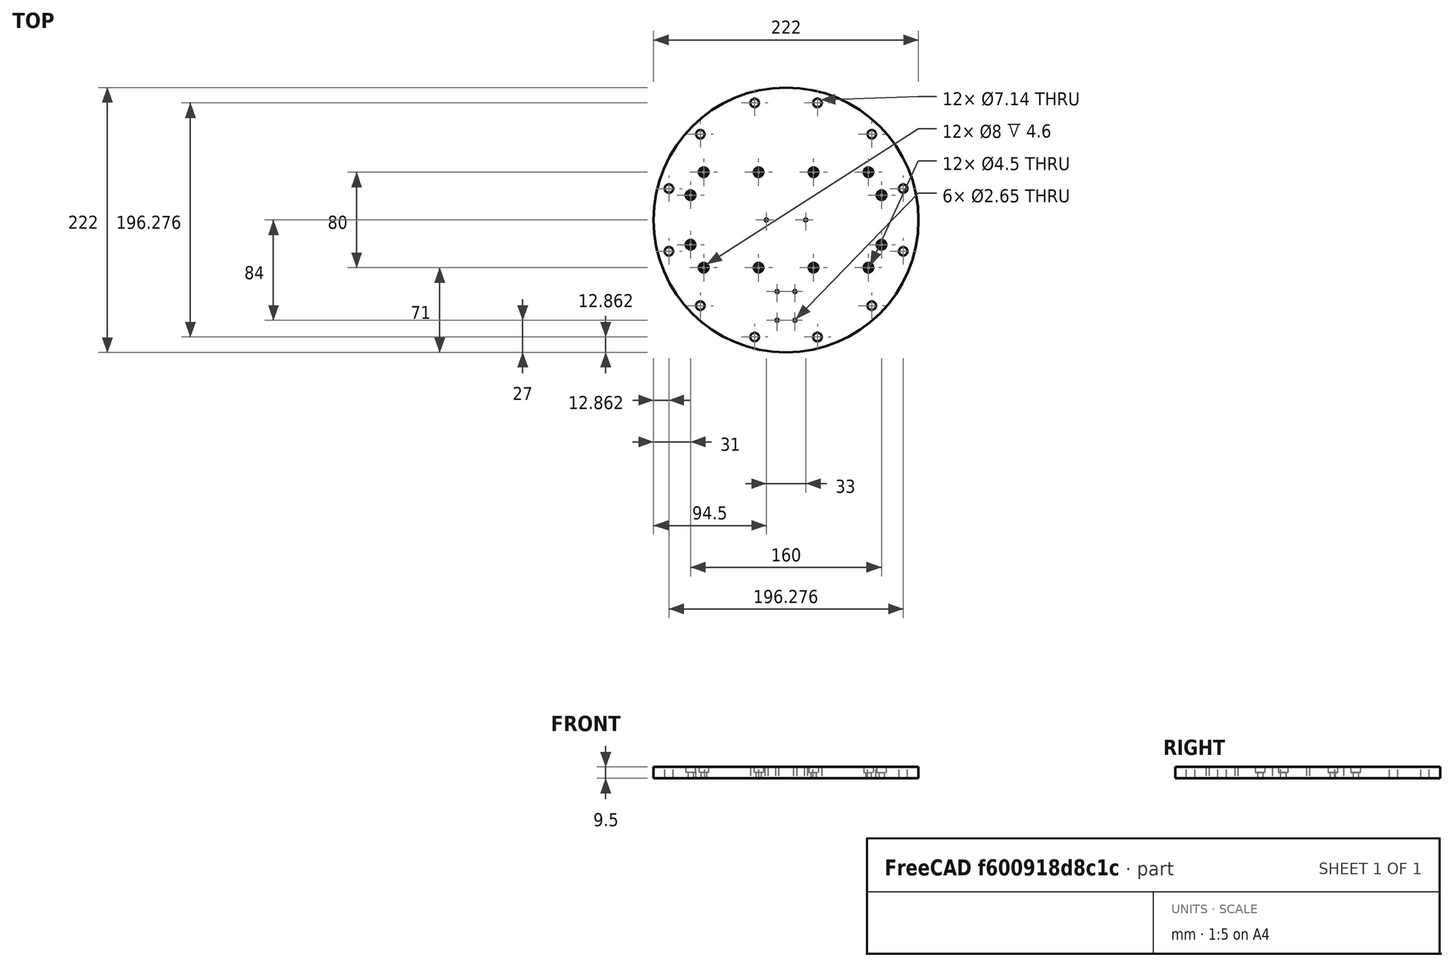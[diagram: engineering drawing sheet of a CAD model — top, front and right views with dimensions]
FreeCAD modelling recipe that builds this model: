
FCSTD DOCUMENT  (FreeCAD 0.19R)
Label: flangle
License: CreativeCommons Attribution-ShareAlike
LicenseURL: http://creativecommons.org/licenses/by-sa/4.0/
objects: TechDraw::DrawViewAnnotation×10, Sketcher::SketchObject×5, PartDesign::Mirrored×4, PartDesign::Hole×3, TechDraw::DrawViewDimension×2, PartDesign::Pad×1, PartDesign::Pocket×1, PartDesign::PolarPattern×1, PartDesign::MultiTransform×1, PartDesign::Body×1, TechDraw::DrawSVGTemplate×1, TechDraw::DrawProjGroupItem×1, TechDraw::DrawProjGroup×1, Spreadsheet::Sheet×1, TechDraw::DrawViewSpreadsheet×1, TechDraw::DrawViewDraft×1, TechDraw::DrawViewPart×1, TechDraw::DrawPage×1
note: 22 computed .brp shape members not serialized (recipe doc carries the construction recipe); baked Part::Feature solids carry a one-line shape summary decoded from their .brp

FEATURE [Sketcher::SketchObject] Sketch
  MapMode = 5
  Support = -> [XY_Plane]
  sketch-geometry (1):
    g0: Circle CenterX=0 CenterY=0 CenterZ=0 NormalX=0 NormalY=0 NormalZ=1 AngleXU=0 Radius=111
  constraints (2):
    c: Coincident(g0,g-1)
    c: Diameter(g0) = 222
FEATURE [PartDesign::Pad] Pad  label="stock"
  Length = 9.5
  Length2 = 100
  Profile = -> Sketch
  Reversed = true
  Type = 0
FEATURE [Sketcher::SketchObject] Sketch001
  MapMode = 5
  Support = -> [XY_Plane]
  sketch-geometry (2):
    g0: Circle CenterX=26.296 CenterY=98.1381 CenterZ=0 NormalX=0 NormalY=0 NormalZ=1 AngleXU=0 Radius=3.57
    g1: LineSegment [constr] StartX=26.296 StartY=98.1381 StartZ=0 EndX=7.1e-15 EndY=0 EndZ=0
  constraints (5):
    c: Diameter(g0) = 7.14
    c: Coincident(g1,g0)
    c: Coincident(g1,g-1)
    c: Angle(g1,g-2) = 0.261799
    c: Distance(g1) = 101.6
FEATURE [PartDesign::Pocket] Pocket  label="mount-hole"
  BaseFeature = -> Pad
  Length = 5
  Length2 = 100
  Profile = -> Sketch001
  Type = 1
FEATURE [PartDesign::PolarPattern] PolarPattern  label="mounting-holes"
  Angle = 360
  Axis = -> Sketch001 [N_Axis]
  BaseFeature = -> Pocket
  Occurrences = 12
  Originals = -> [Pocket]
FEATURE [Sketcher::SketchObject] Sketch002
  MapMode = 5
  Support = -> [XY_Plane]
  sketch-geometry (3):
    g0: Circle CenterX=-80 CenterY=20.75 CenterZ=0 NormalX=0 NormalY=0 NormalZ=1 AngleXU=0 Radius=2.5
    g1: Circle CenterX=-69 CenterY=40 CenterZ=0 NormalX=0 NormalY=0 NormalZ=1 AngleXU=0 Radius=2.5
    g2: Circle CenterX=-23 CenterY=40 CenterZ=0 NormalX=0 NormalY=0 NormalZ=1 AngleXU=0 Radius=2.5
  constraints (9):
    c: Equal(g1,g2)
    c: Equal(g2,g0)
    c: Horizontal(g1,g2)
    c: DistanceX(g0,g-1) = 80
    c: DistanceY(g-1,g0) = 20.75
    c: DistanceY(g-1,g1) = 40
    c: Diameter(g1) = 5
    c: DistanceX(g1,g-1) = 69
    c: DistanceX(g2,g-1) = 23
FEATURE [PartDesign::Hole] Hole
  BaseFeature = -> PolarPattern
  Depth = 25
  DepthType = 1
  Diameter = 4.5
  DrillPoint = 1
  DrillPointAngle = 118
  HoleCutCountersinkAngle = 90
  HoleCutDepth = 4.6
  HoleCutDiameter = 8
  HoleCutType = 1
  ModelActualThread = false
  Profile = -> Sketch002
  Tapered = false
  TaperedAngle = 90
  ThreadAngle = 0
  ThreadClass = 0
  ThreadCutOffInner = 0
  ThreadCutOffOuter = 0
  ThreadDirection = 0
  ThreadFit = 0
  ThreadPitch = 0
  ThreadSize = 0
  ThreadType = 0
  Threaded = false
FEATURE [PartDesign::Mirrored] Mirrored
  MirrorPlane = -> XZ_Plane
FEATURE [PartDesign::Mirrored] Mirrored001
  MirrorPlane = -> Sketch002 [V_Axis]
FEATURE [PartDesign::MultiTransform] MultiTransform
  BaseFeature = -> Hole
  Originals = -> [Hole]
  Transformations = -> [Mirrored,Mirrored001]
FEATURE [Sketcher::SketchObject] Sketch003
  MapMode = 5
  Support = -> [XY_Plane]
  sketch-geometry (2):
    g0: Circle CenterX=-7.5 CenterY=-60 CenterZ=0 NormalX=0 NormalY=0 NormalZ=1 AngleXU=0 Radius=1
    g1: Circle CenterX=-7.5 CenterY=-84 CenterZ=0 NormalX=0 NormalY=0 NormalZ=1 AngleXU=0 Radius=1
  constraints (6):
    c: Vertical(g1,g0)
    c: Equal(g0,g1)
    c: Diameter(g0) = 2
    c: DistanceY(g1,g0) = 24
    c: DistanceX(g0,g-1) = 7.5
    c: DistanceY(g0,g-1) = 60
FEATURE [PartDesign::Hole] Hole001
  BaseFeature = -> MultiTransform
  Depth = 25
  DepthType = 1
  Diameter = 2.65
  DrillPoint = 1
  DrillPointAngle = 118
  HoleCutCountersinkAngle = 90
  HoleCutDepth = 0
  HoleCutDiameter = 3
  HoleCutType = 0
  ModelActualThread = false
  Profile = -> Sketch003
  Tapered = false
  TaperedAngle = 90
  ThreadAngle = 60
  ThreadClass = 0
  ThreadCutOffInner = 0.0378886
  ThreadCutOffOuter = 0.0757772
  ThreadDirection = 0
  ThreadFit = 0
  ThreadPitch = 0.35
  ThreadSize = 9
  ThreadType = 2
  Threaded = true
FEATURE [Sketcher::SketchObject] Sketch004
  MapMode = 5
  Support = -> [XY_Plane]
  sketch-geometry (1):
    g0: Circle CenterX=-16.5 CenterY=0 CenterZ=0 NormalX=0 NormalY=0 NormalZ=1 AngleXU=0 Radius=1.5
  constraints (3):
    c: PointOnObject(g0,g-1)
    c: DistanceX(g0,g-1) = 16.5
    c: Diameter(g0) = 3
FEATURE [PartDesign::Hole] Hole002
  BaseFeature = -> Hole001
  Depth = 25
  DepthType = 1
  Diameter = 2.65
  DrillPoint = 1
  DrillPointAngle = 118
  HoleCutCountersinkAngle = 90
  HoleCutDepth = 0
  HoleCutDiameter = 3
  HoleCutType = 0
  ModelActualThread = false
  Profile = -> Sketch004
  Tapered = false
  TaperedAngle = 90
  ThreadAngle = 60
  ThreadClass = 0
  ThreadCutOffInner = 0.0378886
  ThreadCutOffOuter = 0.0757772
  ThreadDirection = 1
  ThreadFit = 1
  ThreadPitch = 0.35
  ThreadSize = 9
  ThreadType = 2
  Threaded = true
FEATURE [PartDesign::Mirrored] Mirrored002
  BaseFeature = -> Hole002
  MirrorPlane = -> YZ_Plane
  Originals = -> [Hole001]
FEATURE [PartDesign::Mirrored] Mirrored003
  BaseFeature = -> Mirrored002
  MirrorPlane = -> Sketch004 [V_Axis]
  Originals = -> [Hole002]
FEATURE [PartDesign::Body] Body
  Group = -> [Sketch,Pad,Sketch001,Pocket,PolarPattern,Sketch002,Hole,MultiTransform,Mirrored,Mirrored001,Sketch003,Hole001,Sketch004,Hole002,Mirrored002,Mirrored003]
  Origin = -> Origin
  Tip = -> Mirrored003
FEATURE [TechDraw::DrawSVGTemplate] Template
  EditableTexts = Designed_by_Name=A. Ampatzoglou; FC-Date=07/11/2019; FC-SC=1:2; FC-SHEET=1/1; FC-Title=Deployer - Flange; MATERIAL=NOTE-1; REV=B; ROUGHNESS=-; Subtitle=flange; TOLERANCES=DIN ISO 2768 - mk; Weight=~1.0kg
  Height = 210
  Orientation = 1
  Width = 297
FEATURE [TechDraw::DrawProjGroupItem] ProjItem  label="Front"
  CoarseView = false
  Direction = (0,0,1)
  Focus = 100
  HardHidden = false
  IsoCount = 0
  IsoHidden = false
  IsoVisible = false
  LockPosition = true
  Perspective = false
  Rotation = 0
  RotationVector = (1,0,0)
  Scale = 0.5
  ScaleType = 2
  SeamHidden = false
  SeamVisible = false
  SmoothHidden = false
  SmoothVisible = false
  Source = -> [Body]
  Type = 0
  X = 0
  Y = 0
FEATURE [TechDraw::DrawProjGroup] ProjGroup
  Anchor = -> ProjItem
  AutoDistribute = true
  LockPosition = false
  ProjectionType = 1
  Rotation = 0
  Scale = 0.5
  ScaleType = 2
  Source = -> [Body]
  Views = -> [ProjItem]
  X = 99.3124
  Y = 124.964
  spacingX = 15
  spacingY = 15
FEATURE [Spreadsheet::Sheet] Spreadsheet
  cells = A1=TAG; B1=XLOC; C1=YLOC; D1=SIZE; A2=A-1; B2=23; C2=40; D2=⌀4.5 THRU, CBORE ⌀8.0 DEEP 4.6 (M4 DIN912); A3=A-2; B3=69; C3=40; D3=⌀4.5 THRU, CBORE ⌀8.0 DEEP 4.6 (M4 DIN912); A4=A-3; B4=80; C4=20.75; D4=⌀4.5 THRU, CBORE ⌀8.0 DEEP 4.6 (M4 DIN912); A5=B-1; B5=16.5; C5=0; D5=⌀2.5 THRU, Tapping Drill M3x0.5; A6=C-1; B6=7.5; C6=60; D6=⌀2.5 THRU, Tapping Drill M3x0.5; A7=C-2; B7=7.5; C7=84; D7=⌀2.5 THRU, Tapping Drill M3x0.5
FEATURE [TechDraw::DrawViewSpreadsheet] Sheet
  CellEnd = D7
  CellStart = A1
  Font = DejaVu Sans
  LineWidth = 0.35
  LockPosition = false
  Rotation = 0
  Scale = 0.8
  ScaleType = 2
  Source = -> Spreadsheet
  Symbol = <blob: 6284 chars omitted>
  TextSize = 12
  X = 233.125
  Y = 87.5215
FEATURE [TechDraw::DrawViewAnnotation] Annotation
  Font = DejaVu Sans
  LineSpace = 80
  LockPosition = false
  MaxWidth = -1
  Rotation = 0
  ScaleType = 0
  Text = Notes: | 1. Material: Al 7075 | 2. Thickness: 9.5mm | 3.  \u23009/32" x12 THRU Holes are placed | in \u23008.0"\xb10.005" circle | 4. This part is mating with x-plate | and y-plate parts
  TextSize = 6
  TextStyle = 0
  X = 68.1593
  Y = 31.2532
FEATURE [TechDraw::DrawViewDimension] Dimension
  Arbitrary = false
  FormatSpec = ⌀%.2f
  Inverted = false
  LockPosition = false
  MeasureType = 1
  OverTolerance = 0
  References2D = -> [ProjItem]
  Rotation = 0
  ScaleType = 0
  TheoreticalExact = false
  Type = 5
  UnderTolerance = 0
  X = 59.031
  Y = -46.9021
FEATURE [TechDraw::DrawViewAnnotation] Annotation001  label="A-1"
  Font = DejaVu Sans
  LineSpace = 80
  LockPosition = false
  MaxWidth = -1
  Rotation = 0
  ScaleType = 0
  Text = A-1
  TextSize = 6
  TextStyle = 0
  X = 87.5871
  Y = 147.292
FEATURE [TechDraw::DrawViewAnnotation] Annotation002  label="A-2"
  Font = DejaVu Sans
  LineSpace = 80
  LockPosition = false
  MaxWidth = -1
  Rotation = 0
  ScaleType = 0
  Text = A-2
  TextSize = 6
  TextStyle = 0
  X = 64.8546
  Y = 147.034
FEATURE [TechDraw::DrawViewAnnotation] Annotation003  label="A-3"
  Font = DejaVu Sans
  LineSpace = 80
  LockPosition = false
  MaxWidth = -1
  Rotation = 0
  ScaleType = 0
  Text = A-3
  TextSize = 6
  TextStyle = 0
  X = 58.8843
  Y = 138.078
FEATURE [TechDraw::DrawViewAnnotation] Annotation004  label="B-1"
  Font = DejaVu Sans
  LineSpace = 80
  LockPosition = false
  MaxWidth = -1
  Rotation = 0
  ScaleType = 0
  Text = B-1
  TextSize = 6
  TextStyle = 0
  X = 90.9373
  Y = 127.193
FEATURE [TechDraw::DrawViewAnnotation] Annotation005  label="C-1"
  Font = DejaVu Sans
  LineSpace = 80
  LockPosition = false
  MaxWidth = -1
  Rotation = 0
  ScaleType = 0
  Text = C-1
  TextSize = 6
  TextStyle = 0
  X = 87.4696
  Y = 92.5869
FEATURE [TechDraw::DrawViewAnnotation] Annotation006  label="C-2"
  Font = DejaVu Sans
  LineSpace = 80
  LockPosition = false
  MaxWidth = -1
  Rotation = 0
  ScaleType = 0
  Text = C-2
  TextSize = 6
  TextStyle = 0
  X = 87.4897
  Y = 80.7014
FEATURE [TechDraw::DrawViewDraft] DraftView
  Direction = (0,0,1)
  FontSize = 12
  LineSpacing = 10
  LineStyle = Dashdot
  LineWidth = 0.35
  LockPosition = false
  OverrideStyle = false
  Rotation = 0
  Scale = 0.5
  ScaleType = 2
  Symbol = <svg\n	xmlns="http://www.w3.org/2000/svg" version="1.1"\n	xmlns:freecad="http://www.freecadweb.org/wiki/index.php?title=Svg_Namespace">\n<g transform ="scale(1,-1)">\n    <circle cx="-0.0" cy="-0.0" r="101.6" stroke="#191919" stroke-width="0.7 px" style="stroke-width:0.7;stroke-miterlimit:4;stroke-dasharray:0.18,0.1,0.04,0.1;fill:none"/>\n</g>\n\n</svg>
  X = 99.31
  Y = 124.96
FEATURE [TechDraw::DrawViewDimension] Dimension001
  Arbitrary = false
  FormatSpec = ⌀%.2f (Note-3)
  Inverted = false
  LockPosition = false
  MeasureType = 1
  OverTolerance = 0
  References2D = -> [ProjItem]
  Rotation = 0
  ScaleType = 0
  TheoreticalExact = false
  Type = 5
  UnderTolerance = 0
  X = 63.613
  Y = 49.0359
FEATURE [TechDraw::DrawViewAnnotation] Annotation007  label="YLOC"
  Font = DejaVu Sans
  LineSpace = 80
  LockPosition = false
  MaxWidth = -1
  Rotation = 90
  ScaleType = 0
  Text = YLOC
  TextSize = 6
  TextStyle = 0
  X = 97.0181
  Y = 188.869
FEATURE [TechDraw::DrawViewAnnotation] Annotation008  label="XLOC"
  Font = DejaVu Sans
  LineSpace = 80
  LockPosition = false
  MaxWidth = -1
  Rotation = 0
  ScaleType = 0
  Text = XLOC
  TextSize = 6
  TextStyle = 0
  X = 33.8691
  Y = 127.579
FEATURE [TechDraw::DrawViewAnnotation] Annotation009
  Font = DejaVu Sans
  LineSpace = 80
  LockPosition = false
  MaxWidth = -1
  Rotation = 0
  ScaleType = 0
  Text = SCALE 0.2
  TextSize = 6
  TextStyle = 0
  X = 231.302
  Y = 135.562
FEATURE [TechDraw::DrawViewPart] View001
  CoarseView = false
  Direction = (0.093,-0.16,0.983)
  Focus = 100
  HardHidden = false
  IsoCount = 0
  IsoHidden = false
  IsoVisible = false
  LockPosition = false
  Perspective = false
  Rotation = 0
  Scale = 0.2
  ScaleType = 0
  SeamHidden = false
  SeamVisible = false
  SmoothHidden = false
  SmoothVisible = false
  Source = -> [Body]
  X = 231.034
  Y = 173.466
FEATURE [TechDraw::DrawPage] Page
  KeepUpdated = true
  NextBalloonIndex = 1
  ProjectionType = 0
  Template = -> Template
  Views = -> [ProjGroup,Sheet,Annotation,Dimension,Annotation001,Annotation002,Annotation003,Annotation004,Annotation005,Annotation006,DraftView,Dimension001,Annotation007,Annotation008,Annotation009,View001]
